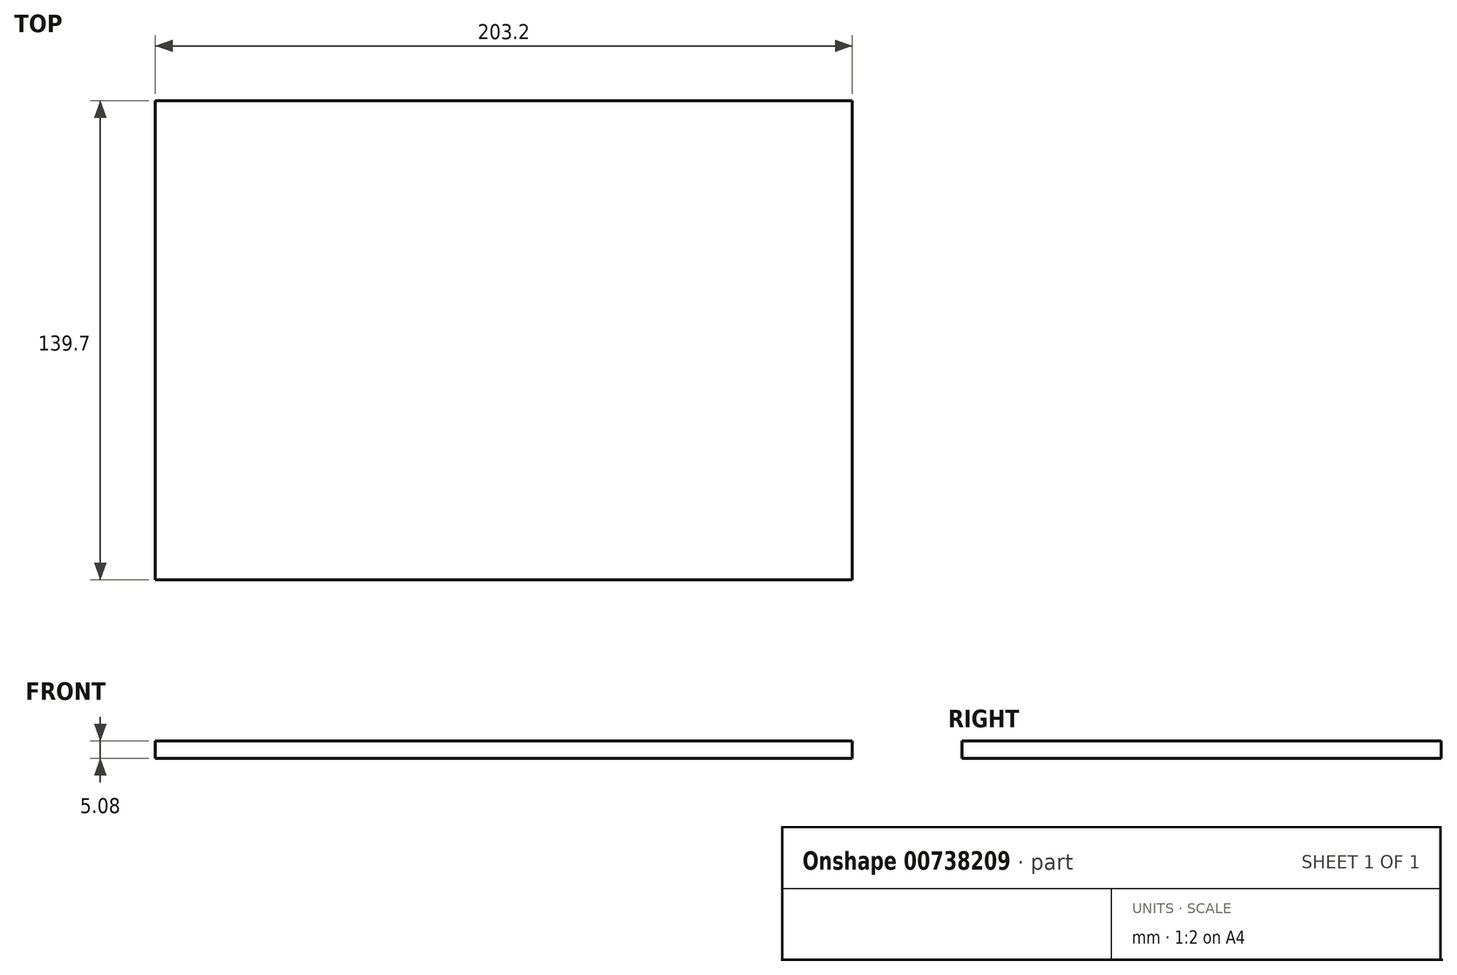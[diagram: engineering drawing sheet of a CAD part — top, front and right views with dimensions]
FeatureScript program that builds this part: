
annotation { "Feature Type Name" : "Feature", "Feature Type Description" : "" }
export const myFeature = defineFeature(function(context is Context, id is Id, definition is map)
    precondition{}
    {
        {
            var Q0;
            Q0=qCreatedBy(makeId("Top.planeOp"),FACE);
            var sketch = newSketch(context, id + "F0", { "sketchPlane" : qUnion([Q0])});
            skLineSegment(sketch, "E0.bottom", {"start": v(-101.6, 69.85) * mm, "end": v(101.6, 69.85) * mm});
            skLineSegment(sketch, "E0.top", {"start": v(-101.6, -69.85) * mm, "end": v(101.6, -69.85) * mm});
            skLineSegment(sketch, "E0.left", {"start": v(-101.6, 69.85) * mm, "end": v(-101.6, -69.85) * mm});
            skLineSegment(sketch, "E0.right", {"start": v(101.6, 69.85) * mm, "end": v(101.6, -69.85) * mm});
            skPoint(sketch, "E0.middle", {"position": v(0, 0) * mm});
            skSolve(sketch);
        }
        {
            var Q0;
            Q0 = qSketchRegion(id + "F0", true);
            extrude(context, id + "F1", {"entities" : qUnion([Q0]), "depth" : 5.08 * mm, "offsetDistance" : 25.4 * mm});
        }
    });
